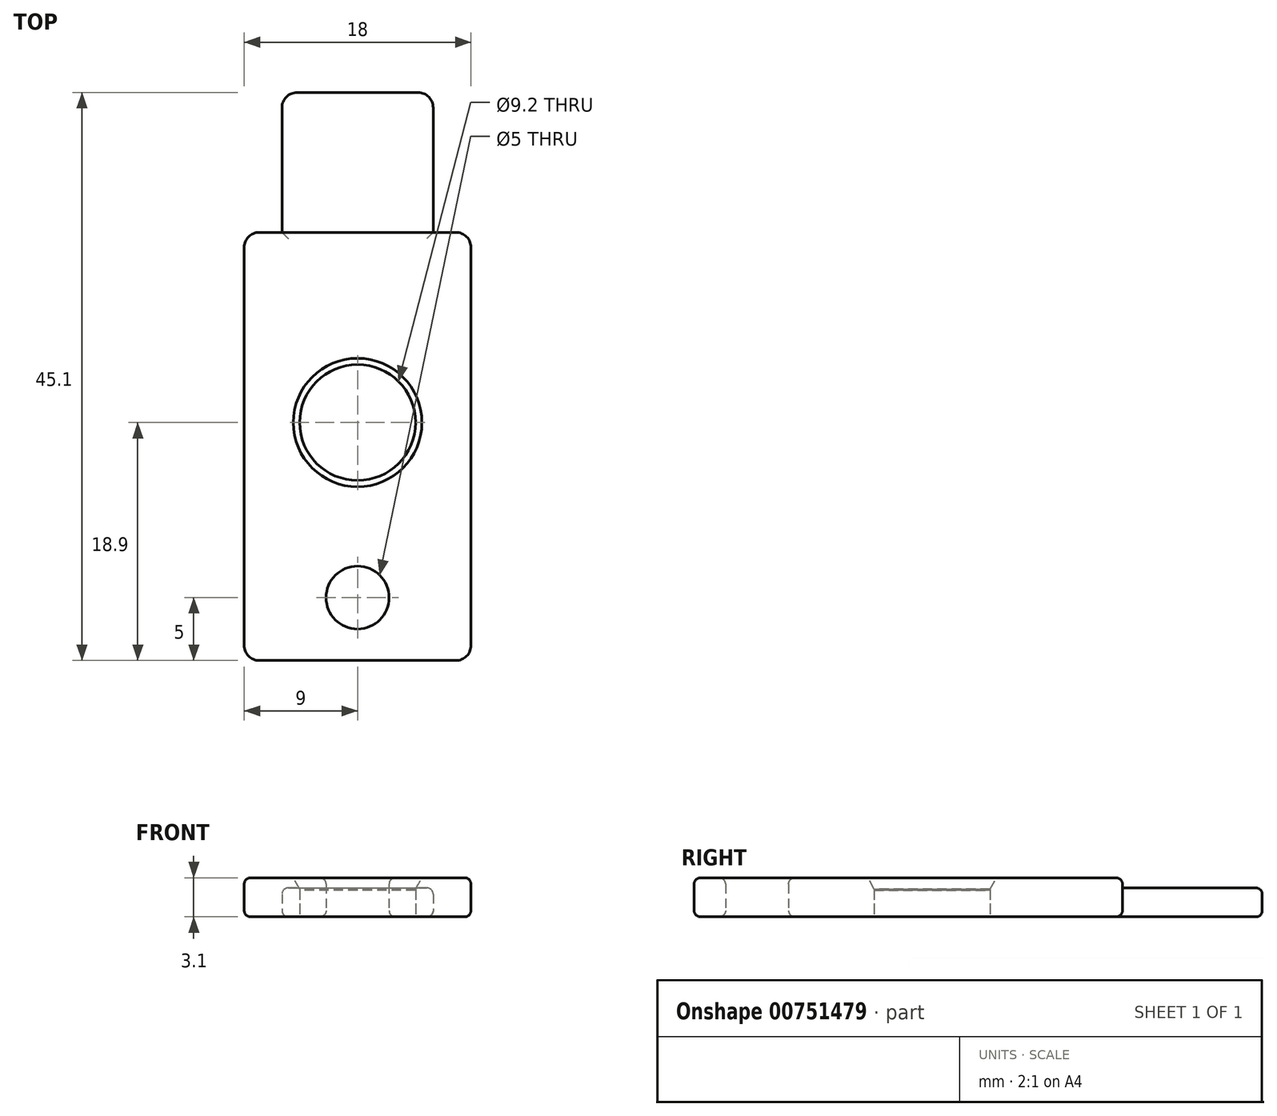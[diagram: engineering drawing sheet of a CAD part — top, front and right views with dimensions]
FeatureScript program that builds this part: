
annotation { "Feature Type Name" : "Feature", "Feature Type Description" : "" }
export const myFeature = defineFeature(function(context is Context, id is Id, definition is map)
    precondition{}
    {
        {
            var Q0;
            Q0=qCreatedBy(makeId("Top.planeOp"),FACE);
            var sketch = newSketch(context, id + "F0", { "sketchPlane" : qUnion([Q0])});
            skLineSegment(sketch, "E0.bottom", {"start": v(1.2, 0) * mm, "end": v(16.8, 0) * mm});
            skLineSegment(sketch, "E0.top", {"start": v(1.2, 34) * mm, "end": v(16.8, 34) * mm});
            skLineSegment(sketch, "E0.left", {"start": v(0, 1.2) * mm, "end": v(0, 32.8) * mm});
            skLineSegment(sketch, "E0.right", {"start": v(18, 1.2) * mm, "end": v(18, 32.8) * mm});
            skLineSegment(sketch, "E1.bottom", {"start": v(3, 34) * mm, "end": v(15, 34) * mm});
            skLineSegment(sketch, "E1.top", {"start": v(4.2, 45.1) * mm, "end": v(13.8, 45.1) * mm});
            skLineSegment(sketch, "E1.left", {"start": v(3, 34) * mm, "end": v(3, 43.9) * mm});
            skLineSegment(sketch, "E1.right", {"start": v(15, 34) * mm, "end": v(15, 43.9) * mm});
            skLineSegment(sketch, "E2", {"start": v(9, 45.1) * mm, "end": v(9, 0) * mm, "construction": true});
            skCircle(sketch, "E3", {"center": v(9, 18.9) * mm, "radius": 4.6 * mm});
            skCircle(sketch, "E4", {"center": v(9, 5) * mm, "radius": 2.5 * mm});
            skPoint(sketch, "E5.visualSharp", {"position": v(3, 45.1) * mm});
            skArc(sketch, "E5.filletArc", {"start": v(4.2, 45.1) * mm, "mid": v(3.35, 44.75) * mm, "end": v(3, 43.9) * mm});
            skPoint(sketch, "E6.visualSharp", {"position": v(15, 45.1) * mm});
            skArc(sketch, "E6.filletArc", {"start": v(15, 43.9) * mm, "mid": v(14.65, 44.75) * mm, "end": v(13.8, 45.1) * mm});
            skPoint(sketch, "E7.visualSharp", {"position": v(18, 34) * mm});
            skArc(sketch, "E7.filletArc", {"start": v(18, 32.8) * mm, "mid": v(17.65, 33.65) * mm, "end": v(16.8, 34) * mm});
            skPoint(sketch, "E8.visualSharp", {"position": v(0, 34) * mm});
            skArc(sketch, "E8.filletArc", {"start": v(1.2, 34) * mm, "mid": v(0.35, 33.65) * mm, "end": v(0, 32.8) * mm});
            skPoint(sketch, "E9.visualSharp", {"position": v(0, 0) * mm});
            skArc(sketch, "E9.filletArc", {"start": v(0, 1.2) * mm, "mid": v(0.35, 0.35) * mm, "end": v(1.2, 0) * mm});
            skPoint(sketch, "E10.visualSharp", {"position": v(18, 0) * mm});
            skArc(sketch, "E10.filletArc", {"start": v(16.8, 0) * mm, "mid": v(17.65, 0.35) * mm, "end": v(18, 1.2) * mm});
            skSolve(sketch);
        }
        {
            var Q0;
            Q0=makeQuery(id+"F0.imprint","IMPRINT",FACE,{"disambiguationData":[TD([[makeQuery(id+"F0.imprint","IMPRINT",EDGE,{"derivedFrom":sQuery(id+"F0.wireOp",EDGE,"E0.bottom")}),1.0]])]});
            extrude(context, id + "F1", {"entities" : qUnion([Q0]), "depth" : 3.1 * mm});
        }
        {
            var Q0;
            Q0=makeQuery(id+"F0.imprint","IMPRINT",FACE,{"disambiguationData":[TD([[makeQuery(id+"F0.imprint","IMPRINT",EDGE,{"derivedFrom":sQuery(id+"F0.wireOp",EDGE,"E1.top")}),-1.0]])]});
            extrude(context, id + "F2", {"entities" : qUnion([Q0]), "operationType" : NewBodyOperationType.ADD, "depth" : 2.3 * mm});
        }
        {
            var Q0;
            Q0=makeQuery(id+"F0.imprint","IMPRINT",FACE,{"disambiguationData":[TD([[makeQuery(id+"F0.imprint","IMPRINT",EDGE,{"derivedFrom":sQuery(id+"F0.wireOp",EDGE,"E3")}),1.0]])]});
            extrude(context, id + "F3", {"entities" : qUnion([Q0]), "depth" : 2.1 * mm});
        }
        {
            var Q0;
            Q0=makeQuery(id+"F1.opExtrude","CAP_EDGE",EDGE,{"disambiguationData":[OSD([sQuery(id+"F0.wireOp",EDGE,"E3")])],"isStart":false});
            chamfer(context, id + "F4", {"entities" : qUnion([Q0]), "chamferType" : ChamferType.TWO_OFFSETS, "width1" : .9 * mm, "oppositeDirection" : false, "width2" : .5 * mm, "tangentPropagation" : true});
        }
        {
            var Q0;
            Q0=makeQuery(id+"F1.opExtrude","CAP_EDGE",EDGE,{"disambiguationData":[OSD([sQuery(id+"F0.wireOp",EDGE,"E0.left")])],"isStart":false});
            var Q1;
            Q1=makeQuery(id+"F1.opExtrude","CAP_EDGE",EDGE,{"disambiguationData":[OSD([sQuery(id+"F0.wireOp",EDGE,"E0.right")])],"isStart":true});
            var Q2;
            Q2=makeQuery(id+"F1.opExtrude","CAP_EDGE",EDGE,{"disambiguationData":[OSD([sQuery(id+"F0.wireOp",EDGE,"E4")])],"isStart":false});
            var Q3;
            Q3=makeQuery(id+"F2.opExtrude","CAP_EDGE",EDGE,{"disambiguationData":[OSD([sQuery(id+"F0.wireOp",EDGE,"E1.right")])],"isStart":false});
            var Q4;
            Q4=makeQuery(id+"F1.opExtrude","CAP_EDGE",EDGE,{"disambiguationData":[OSD([sQuery(id+"F0.wireOp",EDGE,"E4")])],"isStart":true});
            var Q5;
            Q5=makeQuery(id+"F2.opExtrude","CAP_EDGE",EDGE,{"disambiguationData":[OSD([sQuery(id+"F0.wireOp",EDGE,"E1.right")])],"isStart":true});
            fillet(context, id + "F5", {"entities" : qUnion([Q0, Q1, Q2, Q3, Q4, Q5]), "radius" : .5 * mm, "tangentPropagation" : true, "allowEdgeOverflow" : false});
        }
    });
